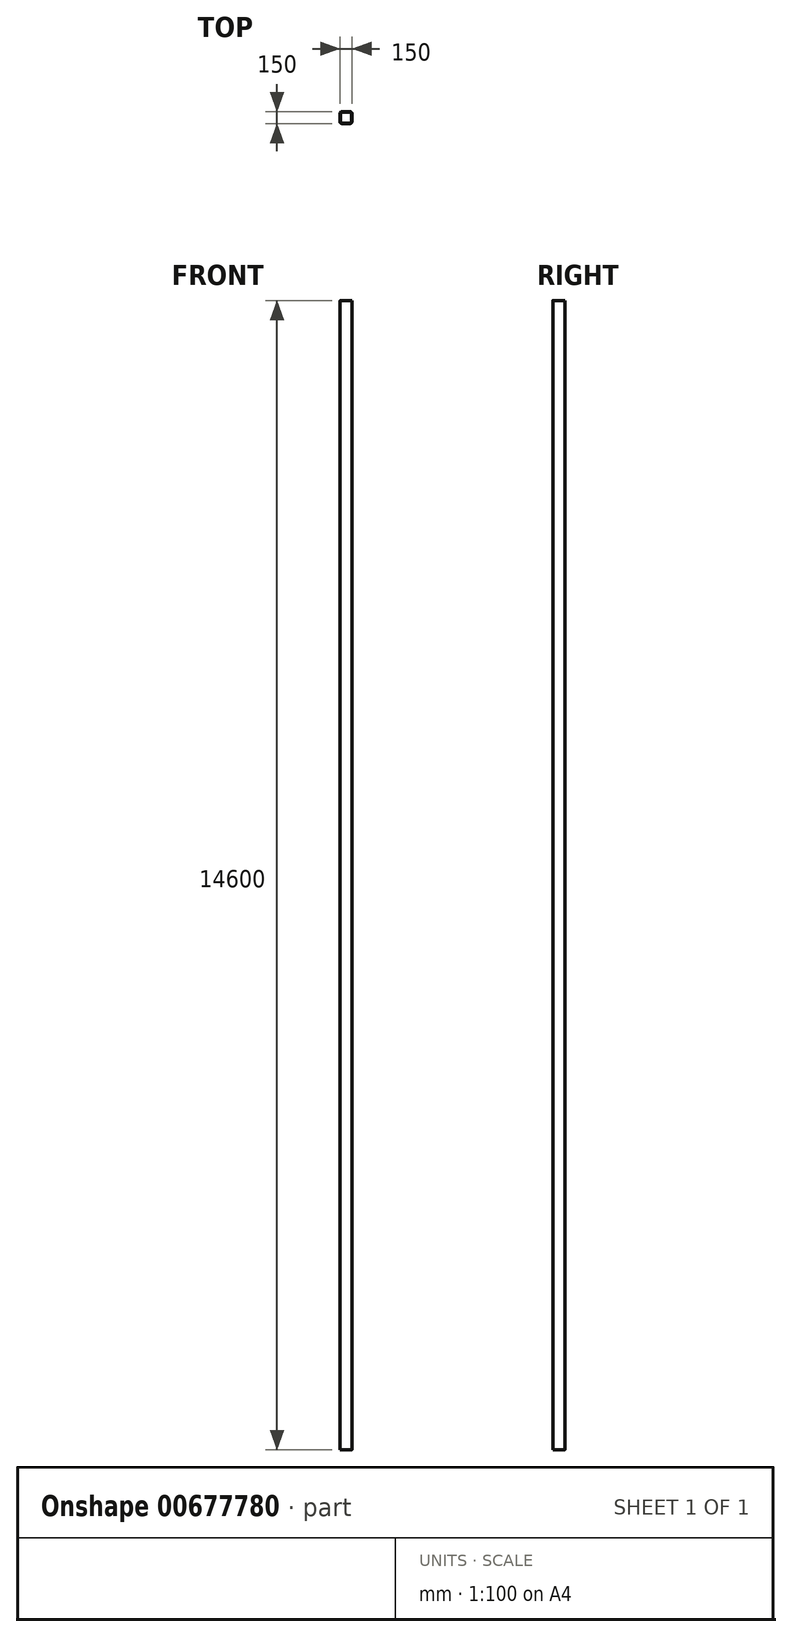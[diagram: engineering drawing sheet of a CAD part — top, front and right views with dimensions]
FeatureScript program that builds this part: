
annotation { "Feature Type Name" : "Feature", "Feature Type Description" : "" }
export const myFeature = defineFeature(function(context is Context, id is Id, definition is map)
    precondition{}
    {
        {
            var Q0;
            Q0=qCreatedBy(makeId("Top.planeOp"),FACE);
            var sketch = newSketch(context, id + "F0", { "sketchPlane" : qUnion([Q0])});
            skLineSegment(sketch, "E0.bottom", {"start": v(55, -75) * mm, "end": v(-55, -75) * mm});
            skLineSegment(sketch, "E0.top", {"start": v(55, 75) * mm, "end": v(-55, 75) * mm});
            skLineSegment(sketch, "E0.left", {"start": v(75, -55) * mm, "end": v(75, 55) * mm});
            skLineSegment(sketch, "E0.right", {"start": v(-75, -55) * mm, "end": v(-75, 55) * mm});
            skPoint(sketch, "E0.middle", {"position": v(0, 0) * mm});
            skPoint(sketch, "E1.visualSharp", {"position": v(-75, 75) * mm});
            skArc(sketch, "E1.filletArc", {"start": v(-55, 75) * mm, "mid": v(-69.14, 69.14) * mm, "end": v(-75, 55) * mm});
            skPoint(sketch, "E2.visualSharp", {"position": v(-75, -75) * mm});
            skArc(sketch, "E2.filletArc", {"start": v(-75, -55) * mm, "mid": v(-69.14, -69.14) * mm, "end": v(-55, -75) * mm});
            skPoint(sketch, "E3.visualSharp", {"position": v(75, -75) * mm});
            skArc(sketch, "E3.filletArc", {"start": v(55, -75) * mm, "mid": v(69.14, -69.14) * mm, "end": v(75, -55) * mm});
            skPoint(sketch, "E4.visualSharp", {"position": v(75, 75) * mm});
            skArc(sketch, "E4.filletArc", {"start": v(75, 55) * mm, "mid": v(69.14, 69.14) * mm, "end": v(55, 75) * mm});
            skArc(sketch, "E5.0", {"start": v(55, -70) * mm, "mid": v(65.6, -65.6) * mm, "end": v(70, -55) * mm});
            skLineSegment(sketch, "E5.1", {"start": v(55, -70) * mm, "end": v(-55, -70) * mm});
            skLineSegment(sketch, "E5.2", {"start": v(70, -55) * mm, "end": v(70, 55) * mm});
            skArc(sketch, "E5.3", {"start": v(-70, -55) * mm, "mid": v(-65.6, -65.6) * mm, "end": v(-55, -70) * mm});
            skArc(sketch, "E5.4", {"start": v(70, 55) * mm, "mid": v(65.6, 65.6) * mm, "end": v(55, 70) * mm});
            skLineSegment(sketch, "E5.5", {"start": v(55, 70) * mm, "end": v(-55, 70) * mm});
            skArc(sketch, "E5.6", {"start": v(-55, 70) * mm, "mid": v(-65.6, 65.6) * mm, "end": v(-70, 55) * mm});
            skLineSegment(sketch, "E5.7", {"start": v(-70, -55) * mm, "end": v(-70, 55) * mm});
            skSolve(sketch);
        }
        {
            var Q0;
            Q0 = qSketchRegion(id + "F0", true);
            extrude(context, id + "F1", {"entities" : qUnion([Q0]), "depth" : 14600 * mm, "offsetDistance" : 25 * mm});
        }
    });
